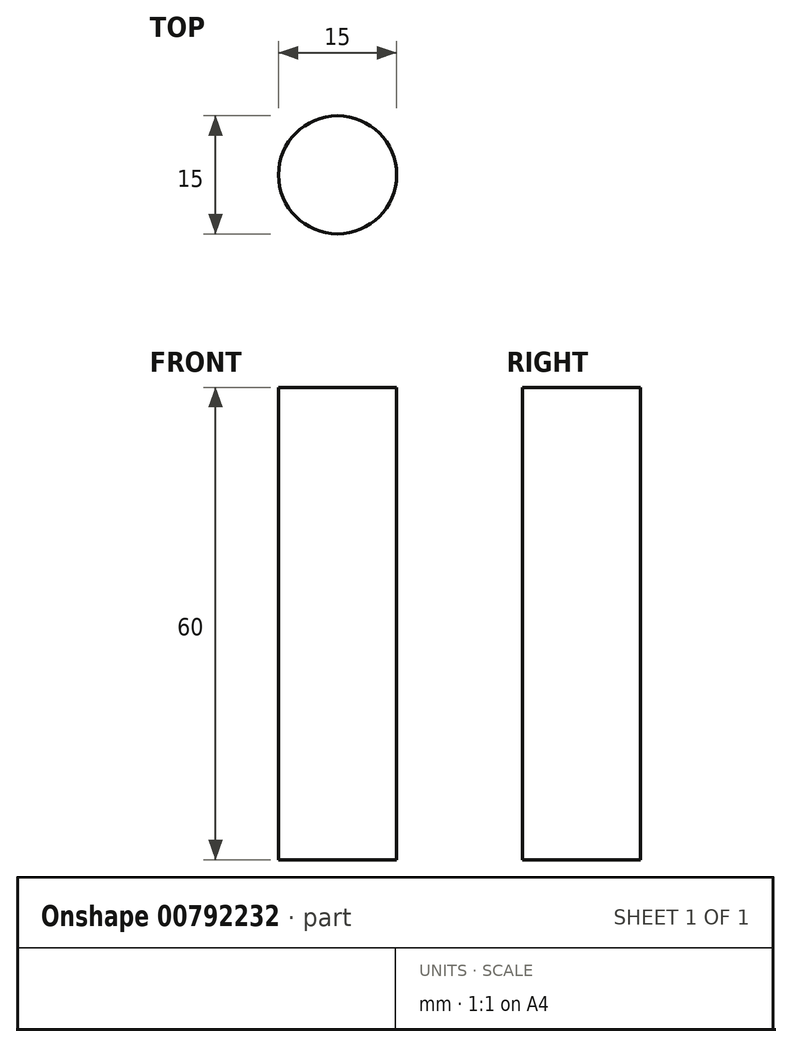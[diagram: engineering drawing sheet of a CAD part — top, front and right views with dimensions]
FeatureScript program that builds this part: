
annotation { "Feature Type Name" : "Feature", "Feature Type Description" : "" }
export const myFeature = defineFeature(function(context is Context, id is Id, definition is map)
    precondition{}
    {
        {
            var Q0;
            Q0=qCreatedBy(makeId("Top.planeOp"),FACE);
            var sketch = newSketch(context, id + "F0", { "sketchPlane" : qUnion([Q0])});
            skCircle(sketch, "E0", {"center": v(0, 0) * mm, "radius": 7.5 * mm});
            skSolve(sketch);
        }
        {
            var Q0;
            Q0=makeQuery(id+"F0.imprint","IMPRINT",FACE,{"disambiguationData":[TD([[makeQuery(id+"F0.imprint","IMPRINT",EDGE,{"derivedFrom":sQuery(id+"F0.wireOp",EDGE,"E0")}),1.0]])]});
            extrude(context, id + "F1", {"entities" : qUnion([Q0]), "depth" : 60 * mm, "offsetDistance" : 25 * mm});
        }
    });
